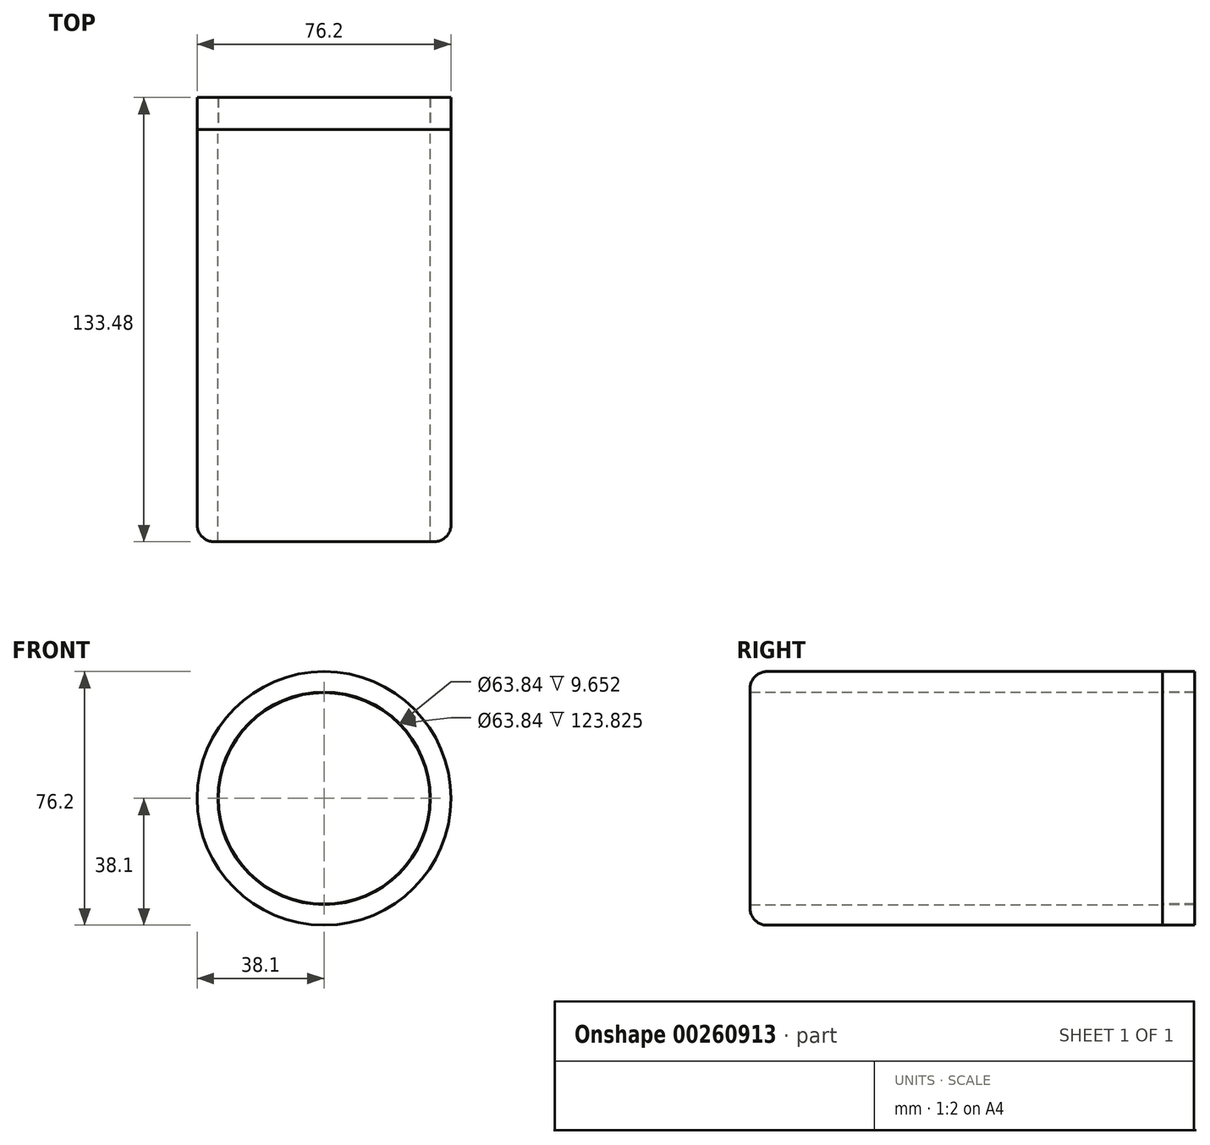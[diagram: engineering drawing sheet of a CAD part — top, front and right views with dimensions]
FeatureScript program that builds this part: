
annotation { "Feature Type Name" : "Feature", "Feature Type Description" : "" }
export const myFeature = defineFeature(function(context is Context, id is Id, definition is map)
    precondition{}
    {
        {
            var Q0;
            Q0=qCreatedBy(makeId("Front.planeOp"),FACE);
            var sketch = newSketch(context, id + "F0", { "sketchPlane" : qUnion([Q0])});
            skCircle(sketch, "E0", {"center": v(0, 0) * mm, "radius": 38.1 * mm});
            skCircle(sketch, "E1", {"center": v(0, 0) * mm, "radius": 31.75 * mm});
            skCircle(sketch, "E2", {"center": v(0, 0) * mm, "radius": 31.92 * mm});
            skSolve(sketch);
        }
        {
            var Q0;
            Q0=makeQuery(id+"F0.imprint","IMPRINT",FACE,{"disambiguationData":[TD([[makeQuery(id+"F0.imprint","IMPRINT",EDGE,{"derivedFrom":sQuery(id+"F0.wireOp",EDGE,"E0")}),1.0]])]});
            extrude(context, id + "F1", {"entities" : qUnion([Q0]), "depth" : 123.82 * mm});
        }
        {
            var Q0;
            Q0=makeQuery(id+"F1.opExtrude","CAP_EDGE",EDGE,{"disambiguationData":[OSD([sQuery(id+"F0.wireOp",EDGE,"E0")])],"isStart":false});
            fillet(context, id + "F2", {"entities" : qUnion([Q0]), "radius" : 5.08 * mm, "tangentPropagation" : true, "allowEdgeOverflow" : false});
        }
        {
            var Q0;
            Q0=makeQuery(id+"F0.imprint","IMPRINT",FACE,{"disambiguationData":[TD([[makeQuery(id+"F0.imprint","IMPRINT",EDGE,{"derivedFrom":sQuery(id+"F0.wireOp",EDGE,"E1")}),1.0]])]});
            var Q1;
            Q1=makeQuery(id+"F0.imprint","IMPRINT",FACE,{"disambiguationData":[TD([[makeQuery(id+"F0.imprint","IMPRINT",EDGE,{"derivedFrom":sQuery(id+"F0.wireOp",EDGE,"E0")}),1.0]])]});
            extrude(context, id + "F3", {"entities" : qUnion([Q0, Q1]), "oppositeDirection" : true, "depth" : 9.65 * mm});
        }
    });
